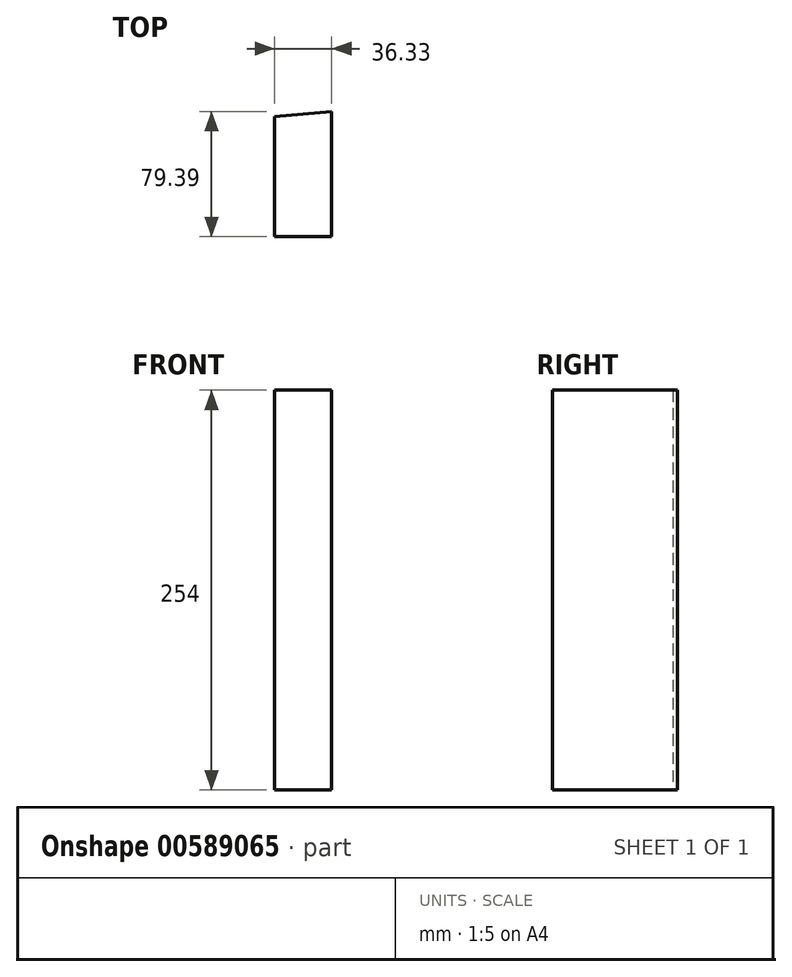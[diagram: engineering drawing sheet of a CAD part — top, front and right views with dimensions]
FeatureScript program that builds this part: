
annotation { "Feature Type Name" : "Feature", "Feature Type Description" : "" }
export const myFeature = defineFeature(function(context is Context, id is Id, definition is map)
    precondition{}
    {
        {
            var Q0;
            Q0=qCreatedBy(makeId("Top.planeOp"),FACE);
            var sketch = newSketch(context, id + "F0", { "sketchPlane" : qUnion([Q0])});
            skLineSegment(sketch, "E0", {"start": v(-115.4, 49.13) * mm, "end": v(-115.4, -27.16) * mm});
            skLineSegment(sketch, "E1", {"start": v(-115.4, -27.16) * mm, "end": v(-79.08, -27.16) * mm});
            skLineSegment(sketch, "E2", {"start": v(-79.08, -27.16) * mm, "end": v(-79.08, 52.23) * mm});
            skLineSegment(sketch, "E3", {"start": v(-79.08, 52.23) * mm, "end": v(-115.4, 49.13) * mm});
            skSolve(sketch);
        }
        {
            var Q0;
            Q0 = qSketchRegion(id + "F0", true);
            extrude(context, id + "F1", {"entities" : qUnion([Q0]), "depth" : 254 * mm, "offsetDistance" : 25.4 * mm});
        }
    });
